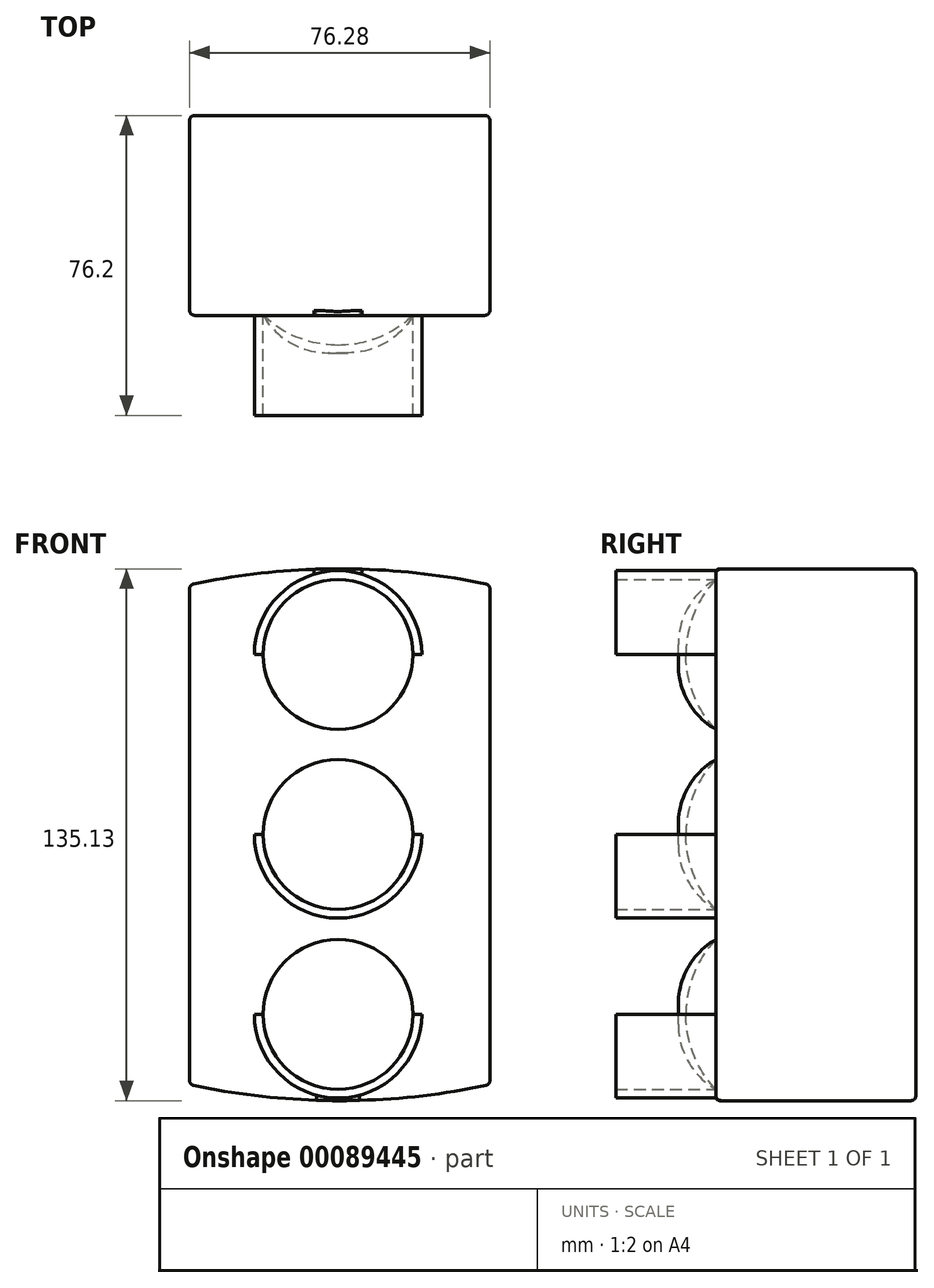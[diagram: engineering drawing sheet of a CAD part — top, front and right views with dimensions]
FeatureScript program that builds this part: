
annotation { "Feature Type Name" : "Feature", "Feature Type Description" : "" }
export const myFeature = defineFeature(function(context is Context, id is Id, definition is map)
    precondition{}
    {
        {
            var Q0;
            Q0=qCreatedBy(makeId("Front.planeOp"),FACE);
            var sketch = newSketch(context, id + "F0", { "sketchPlane" : qUnion([Q0])});
            skLineSegment(sketch, "E0", {"start": v(-49.84, 56.43) * mm, "end": v(-49.84, -70.57) * mm});
            skLineSegment(sketch, "E1", {"start": v(26.44, 56.43) * mm, "end": v(26.44, -70.57) * mm});
            skCircle(sketch, "E2", {"center": v(-12.13, 38.72) * mm, "radius": 19.05 * mm});
            skCircle(sketch, "E3", {"center": v(-12.13, -7) * mm, "radius": 19.05 * mm});
            skCircle(sketch, "E4", {"center": v(-12.13, -52.72) * mm, "radius": 19.05 * mm});
            skArc(sketch, "E5", {"start": v(26.44, 56.43) * mm, "mid": v(-11.7, 60.5) * mm, "end": v(-49.84, 56.43) * mm});
            skArc(sketch, "E6", {"start": v(-49.84, -70.57) * mm, "mid": v(-11.7, -74.64) * mm, "end": v(26.44, -70.57) * mm});
            skSolve(sketch);
        }
        {
            var Q0;
            Q0=makeQuery(id+"F0.imprint","IMPRINT",FACE,{"disambiguationData":[TD([[makeQuery(id+"F0.imprint","IMPRINT",EDGE,{"derivedFrom":sQuery(id+"F0.wireOp",EDGE,"E0")}),1.0]])]});
            extrude(context, id + "F1", {"entities" : qUnion([Q0]), "depth" : 50.8 * mm});
        }
        {
            var Q0;
            Q0=makeQuery(id+"F0.imprint","IMPRINT",FACE,{"disambiguationData":[TD([[makeQuery(id+"F0.imprint","IMPRINT",EDGE,{"derivedFrom":sQuery(id+"F0.wireOp",EDGE,"E2")}),1.0]])]});
            var Q1;
            Q1=makeQuery(id+"F0.imprint","IMPRINT",FACE,{"disambiguationData":[TD([[makeQuery(id+"F0.imprint","IMPRINT",EDGE,{"derivedFrom":sQuery(id+"F0.wireOp",EDGE,"E3")}),1.0]])]});
            var Q2;
            Q2=makeQuery(id+"F0.imprint","IMPRINT",FACE,{"disambiguationData":[TD([[makeQuery(id+"F0.imprint","IMPRINT",EDGE,{"derivedFrom":sQuery(id+"F0.wireOp",EDGE,"E4")}),1.0]])]});
            extrude(context, id + "F2", {"entities" : qUnion([Q0, Q1, Q2]), "operationType" : NewBodyOperationType.ADD, "depth" : 58.42 * mm});
        }
        {
            var Q0;
            Q0=makeQuery(id+"F2.opExtrude","CAP_FACE",FACE,{"disambiguationData":[OSD([sQuery(id+"F0.wireOp",EDGE,"E2")])],"isStart":false});
            var Q1;
            Q1=makeQuery(id+"F2.opExtrude","CAP_FACE",FACE,{"disambiguationData":[OSD([sQuery(id+"F0.wireOp",EDGE,"E3")])],"isStart":false});
            var Q2;
            Q2=makeQuery(id+"F2.opExtrude","CAP_FACE",FACE,{"disambiguationData":[OSD([sQuery(id+"F0.wireOp",EDGE,"E4")])],"isStart":false});
            fillet(context, id + "F3", {"entities" : qUnion([Q0, Q1, Q2]), "radius" : 27.6 * mm, "tangentPropagation" : true, "allowEdgeOverflow" : false});
        }
        {
            var Q0;
            Q0=makeQuery(id+"F1.opExtrude","CAP_FACE",FACE,{"disambiguationData":[OSD([sQuery(id+"F0.wireOp",EDGE,"E0"),sQuery(id+"F0.wireOp",EDGE,"E1"),sQuery(id+"F0.wireOp",EDGE,"E2"),sQuery(id+"F0.wireOp",EDGE,"E3"),sQuery(id+"F0.wireOp",EDGE,"E4"),sQuery(id+"F0.wireOp",EDGE,"E5"),sQuery(id+"F0.wireOp",EDGE,"E6")])],"isStart":false});
            var sketch = newSketch(context, id + "F4", { "sketchPlane" : qUnion([Q0])});
            skCircle(sketch, "E7.0", {"center": v(-12.13, 38.72) * mm, "radius": 19.05 * mm});
            skCircle(sketch, "E8", {"center": v(-12.13, 38.72) * mm, "radius": 21.28 * mm});
            skLineSegment(sketch, "E9", {"start": v(-33.4, 38.72) * mm, "end": v(-31.18, 38.72) * mm});
            skLineSegment(sketch, "E10", {"start": v(-31.18, 38.72) * mm, "end": v(9.15, 38.72) * mm});
            skCircle(sketch, "E11", {"center": v(-12.13, -7) * mm, "radius": 21.27 * mm});
            skCircle(sketch, "E12", {"center": v(-12.13, -52.72) * mm, "radius": 21.27 * mm});
            skCircle(sketch, "E13.0", {"center": v(-12.13, -7) * mm, "radius": 19.05 * mm});
            skCircle(sketch, "E14.0", {"center": v(-12.13, -52.72) * mm, "radius": 19.05 * mm});
            skLineSegment(sketch, "E15", {"start": v(9.14, -7) * mm, "end": v(-33.4, -7) * mm});
            skLineSegment(sketch, "E16", {"start": v(9.14, -52.72) * mm, "end": v(-33.4, -52.72) * mm});
            skSolve(sketch);
        }
        {
            var Q0;
            {var subQ1=sQuery(id+"F4.wireOp",EDGE,"E9");Q0=makeQuery(id+"F4.imprint","IMPRINT",FACE,{"disambiguationData":[TD([[makeQuery(id+"F4.imprint","IMPRINT",EDGE,{"derivedFrom":subQ1}),1.0]])]});}
            var Q1;
            {var subQ0=sQuery(id+"F4.wireOp",EDGE,"E15");var subQ1=sQuery(id+"F4.wireOp",EDGE,"E11");var subQ2=makeQuery(id+"F4.imprint","INTERSECT",VERTEX,{"disambiguationData":[OD(0.0)],"derivedFrom":[subQ1,subQ0]});Q1=makeQuery(id+"F4.imprint","IMPRINT",FACE,{"disambiguationData":[TD([[makeQuery(id+"F4.imprint","IMPRINT",EDGE,{"disambiguationData":[TD([[subQ2,-1.0]])],"derivedFrom":subQ1}),1.0]])]});}
            var Q2;
            {var subQ0=sQuery(id+"F4.wireOp",EDGE,"E16");var subQ1=sQuery(id+"F4.wireOp",EDGE,"E12");var subQ2=makeQuery(id+"F4.imprint","INTERSECT",VERTEX,{"disambiguationData":[OD(0.0)],"derivedFrom":[subQ1,subQ0]});Q2=makeQuery(id+"F4.imprint","IMPRINT",FACE,{"disambiguationData":[TD([[makeQuery(id+"F4.imprint","IMPRINT",EDGE,{"disambiguationData":[TD([[subQ2,-1.0]])],"derivedFrom":subQ1}),1.0]])]});}
            extrude(context, id + "F5", {"entities" : qUnion([Q0, Q1, Q2]), "operationType" : NewBodyOperationType.ADD, "depth" : 25.4 * mm});
        }
        {
            var Q0;
            Q0=makeQuery(id+"F1.opExtrude","CAP_EDGE",EDGE,{"disambiguationData":[OSD([sQuery(id+"F0.wireOp",EDGE,"E1")])],"isStart":false});
            var Q1;
            Q1=makeQuery(id+"F1.opExtrude","CAP_EDGE",EDGE,{"disambiguationData":[OSD([sQuery(id+"F0.wireOp",EDGE,"E6")])],"isStart":false});
            var Q2;
            Q2=makeQuery(id+"F1.opExtrude","SWEPT_EDGE",EDGE,{"disambiguationData":[OSD([sQuery(id+"F0.wireOp",EDGE,"E1"),sQuery(id+"F0.wireOp",EDGE,"E6")])]});
            var Q3;
            Q3=makeQuery(id+"F1.opExtrude","SWEPT_EDGE",EDGE,{"disambiguationData":[OSD([sQuery(id+"F0.wireOp",EDGE,"E0"),sQuery(id+"F0.wireOp",EDGE,"E6")])]});
            var Q4;
            Q4=makeQuery(id+"F1.opExtrude","CAP_EDGE",EDGE,{"disambiguationData":[OSD([sQuery(id+"F0.wireOp",EDGE,"E6")])],"isStart":true});
            var Q5;
            Q5=makeQuery(id+"F1.opExtrude","CAP_EDGE",EDGE,{"disambiguationData":[OSD([sQuery(id+"F0.wireOp",EDGE,"E1")])],"isStart":true});
            var Q6;
            Q6=makeQuery(id+"F1.opExtrude","CAP_EDGE",EDGE,{"disambiguationData":[OSD([sQuery(id+"F0.wireOp",EDGE,"E0")])],"isStart":false});
            var Q7;
            Q7=makeQuery(id+"F1.opExtrude","CAP_EDGE",EDGE,{"disambiguationData":[OSD([sQuery(id+"F0.wireOp",EDGE,"E0")])],"isStart":true});
            var Q8;
            Q8=makeQuery(id+"F1.opExtrude","CAP_EDGE",EDGE,{"disambiguationData":[OSD([sQuery(id+"F0.wireOp",EDGE,"E5")])],"isStart":false});
            var Q9;
            Q9=makeQuery(id+"F1.opExtrude","CAP_EDGE",EDGE,{"disambiguationData":[OSD([sQuery(id+"F0.wireOp",EDGE,"E5")])],"isStart":true});
            var Q10;
            Q10=makeQuery(id+"F1.opExtrude","SWEPT_EDGE",EDGE,{"disambiguationData":[OSD([sQuery(id+"F0.wireOp",EDGE,"E0"),sQuery(id+"F0.wireOp",EDGE,"E5")])]});
            var Q11;
            Q11=makeQuery(id+"F1.opExtrude","SWEPT_EDGE",EDGE,{"disambiguationData":[OSD([sQuery(id+"F0.wireOp",EDGE,"E1"),sQuery(id+"F0.wireOp",EDGE,"E5")])]});
            fillet(context, id + "F6", {"entities" : qUnion([Q0, Q1, Q2, Q3, Q4, Q5, Q6, Q7, Q8, Q9, Q10, Q11]), "radius" : 1.27 * mm, "tangentPropagation" : true, "allowEdgeOverflow" : false});
        }
        {
            var Q0;
            Q0=makeQuery(id+"F1.opExtrude","CAP_FACE",FACE,{"disambiguationData":[OSD([sQuery(id+"F0.wireOp",EDGE,"E0"),sQuery(id+"F0.wireOp",EDGE,"E1"),sQuery(id+"F0.wireOp",EDGE,"E2"),sQuery(id+"F0.wireOp",EDGE,"E3"),sQuery(id+"F0.wireOp",EDGE,"E4"),sQuery(id+"F0.wireOp",EDGE,"E5"),sQuery(id+"F0.wireOp",EDGE,"E6")])],"isStart":false});
            var sketch = newSketch(context, id + "F7", { "sketchPlane" : qUnion([Q0])});
            skArc(sketch, "E17.0", {"start": v(-31.18, 38.72) * mm, "mid": v(-12.13, 19.67) * mm, "end": v(6.92, 38.72) * mm});
            skArc(sketch, "E18.0", {"start": v(6.92, 38.72) * mm, "mid": v(-12.13, 57.77) * mm, "end": v(-31.18, 38.72) * mm});
            skArc(sketch, "E19.0", {"start": v(6.92, -7) * mm, "mid": v(-12.13, 12.05) * mm, "end": v(-31.18, -7) * mm});
            skArc(sketch, "E20.0", {"start": v(-31.18, -7) * mm, "mid": v(-12.13, -26.05) * mm, "end": v(6.92, -7) * mm});
            skArc(sketch, "E21.0", {"start": v(6.92, -52.72) * mm, "mid": v(-12.13, -33.67) * mm, "end": v(-31.18, -52.72) * mm});
            skArc(sketch, "E22.0", {"start": v(-31.18, -52.72) * mm, "mid": v(-12.13, -71.77) * mm, "end": v(6.92, -52.72) * mm});
            skSolve(sketch);
        }
        {
            var Q0;
            Q0 = qSketchRegion(id + "F7", true);
            extrude(context, id + "F8", {"entities" : qUnion([Q0]), "depth" : 9.52 * mm});
        }
        {
            var Q0;
            Q0=makeQuery(id+"F8.opExtrude","CAP_FACE",FACE,{"disambiguationData":[OSD([sQuery(id+"F7.wireOp",EDGE,"E17.0"),sQuery(id+"F7.wireOp",EDGE,"E18.0")])],"isStart":false});
            var Q1;
            Q1=makeQuery(id+"F8.opExtrude","CAP_EDGE",EDGE,{"disambiguationData":[OSD([sQuery(id+"F7.wireOp",EDGE,"E19.0"),sQuery(id+"F7.wireOp",EDGE,"E20.0")])],"isStart":false});
            var Q2;
            Q2=makeQuery(id+"F8.opExtrude","CAP_EDGE",EDGE,{"disambiguationData":[OSD([sQuery(id+"F7.wireOp",EDGE,"E21.0"),sQuery(id+"F7.wireOp",EDGE,"E22.0")])],"isStart":false});
            fillet(context, id + "F9", {"entities" : qUnion([Q0, Q1, Q2]), "radius" : 19.05 * mm, "tangentPropagation" : true, "allowEdgeOverflow" : false});
        }
    });
